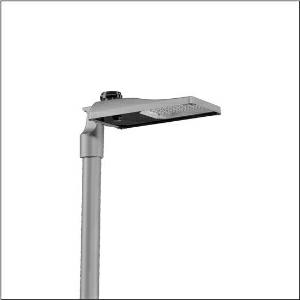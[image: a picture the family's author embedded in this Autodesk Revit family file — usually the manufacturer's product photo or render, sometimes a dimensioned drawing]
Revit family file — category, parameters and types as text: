
# Revit family: streetlight_sl_31_mini___st1_0a_5xh6d35m08ga_0c89
name_source: partatom
category: Lighting Fixtures
units: mm (PartAtom-declared; Revit-internal decimal feet)

## family parameters
Cut with Voids When Loaded = No
Host = Face
Light Source = No
Part Type = Normal
Room Calculation Point = No
Round Connector Dimension = Use Diameter
Shared = No

## types (1)
- --- (1 x LED, 5880 lm, 39.3 W, 3000K)
    Apparent Load = 39 VA
    CIE Flux Codes = 37 72 97 100 100
    Color Rendering = 70
    Color Temperature = 3000K
    Default Elevation = 1800 mm
    Description = Streetlight SL 31 mini NEMA (7pin), Desk-Remote mast luminaire for post-top, side-entry; light control with lens of PMMA; light distribution: ST1.0a, direct asymmetric distribution, for standard-compliant lighting for roads and squares; LED: luminous flux: 5.880lm, light colour: 730, colour temperature: 3000K; luminous efficacy: 149,6lm/W; control: pre-setting: linear dimming characteristic, flexible luminous flux parameterisation, time-dependent luminous flux control, constant luminous flux control, intelligent temperature release in ECG and LED module, overheat protection; luminaire housing, of diecast aluminium, SITECO metallic grey (DB 702S), corrosivity category C5 high according to DIN EN ISO 12944; cover of toughened safety glass, transparent, opened without tools; mast flange of diecast aluminium, SITECO metallic grey (DB 702S), spigot size: 76/60mm, mast flange included unmounted; cable length: 6,5m, connection cable pre-assembled; mains connection: 220..240V, AC, 50/60Hz; power consumption (at start of service life): 39,3W / (at end of service life): 40,7W / (with reduced operation 50%): 18,1W; protection rating (complete): IP66; insulation class (complete): insulation class I (protective earthing); impact resistance: IK09; certification: CE, ENEC, ENEC+, VDE, UKCA; permissible operating ambient temperature for outdoor applications: -40..+50°C; packaging unit: 1 piece

Light Distribution: ST1.0a
    Height = 76 mm
    Lamp = 1 x LED
    Lamp Light Flux = 5880 lm
    Lamp Power = 39.3 W
    Lamp count = 1
    Length = 547 mm
    Luminous efficacy = 150 lm/W
    Manufacturer = Siteco
    ModVariant = No
    Model = 5XH6D35M08GA
    Number of Poles = 1
    OnlyDefault = Yes
    Power Factor = 1
    Product Name = Streetlight SL 31 mini | ST1.0a
    Product group = mast luminaire | pylon top
    ProductGroupID = 6100
    Protection Class = Protection class I
    Protection Degree = IP 66
    RLX_Detail_Level = 1
    RLX_Emergency_Light_Flux = 0 lm
    RLX_Emergency_Type = 0
    RLX_Emergency_Type_DB = No
    RlxData = <blob elided: 40221 chars, md5=7fda8d62>
    Socket = socket
    Standby Power = 0 W
    System Light Flux = 5880 lm
    System Power = 39 W
    Type Comments = factory setting: luminous flux: 100 % | dim-lin: 254 | 798 mA
    Type Image = l_1300324.jpg
    URL = http://relux.com
    VarID = @adj_060389
    Voltage = 0 V
    Weight = 0.00 kg
    Width = 265 mm

## geometry (parser evidence)
native form markers: Blend x4, Sweep x10
no freeform markers — native parametric forms only
